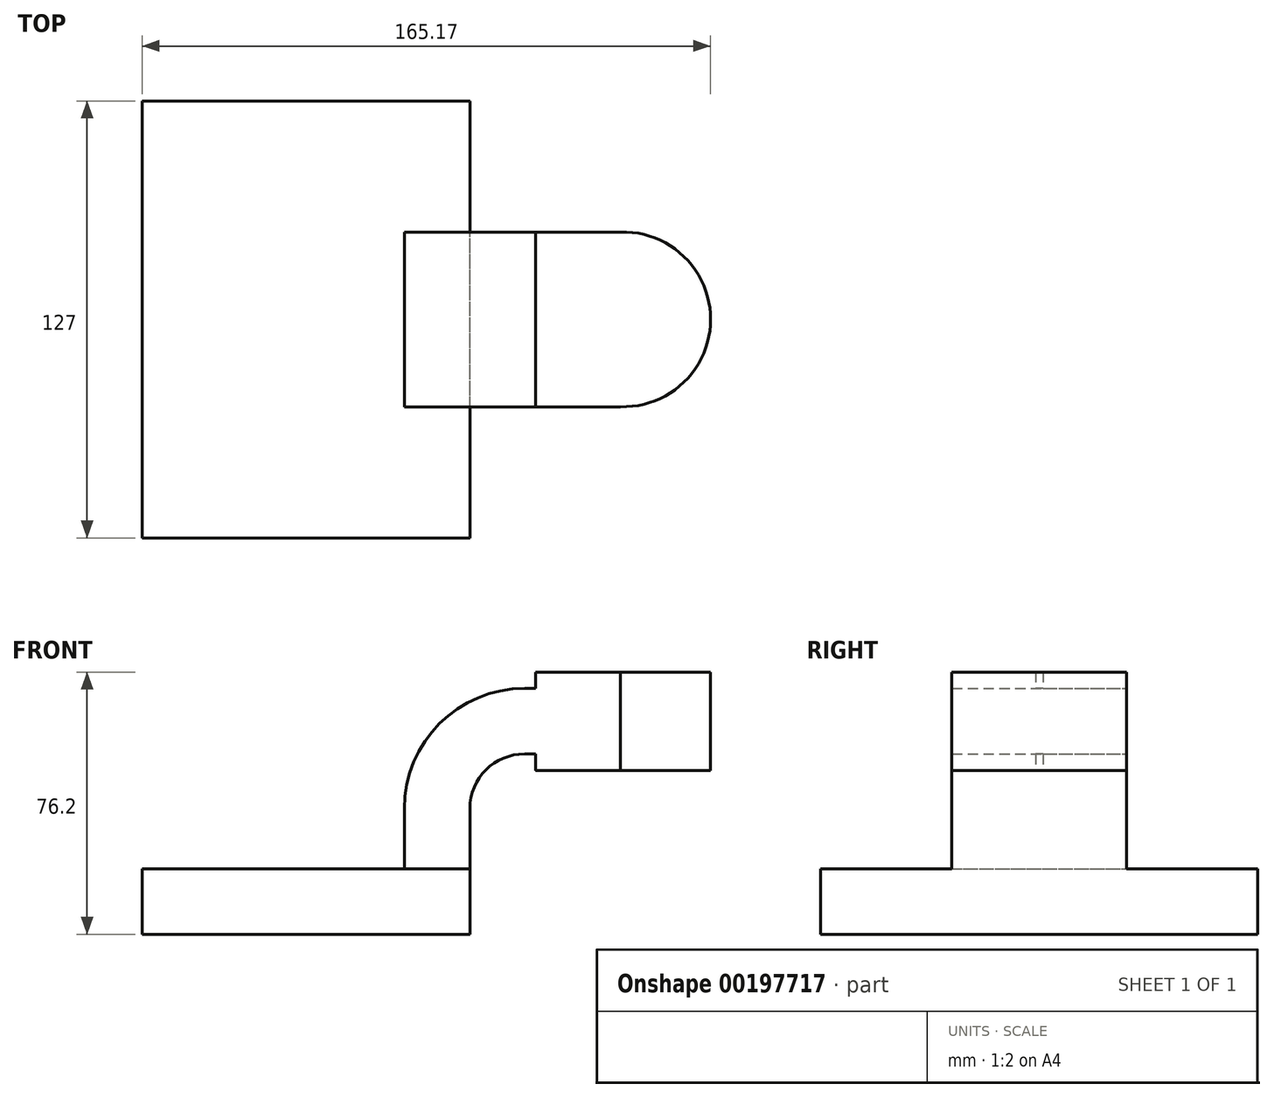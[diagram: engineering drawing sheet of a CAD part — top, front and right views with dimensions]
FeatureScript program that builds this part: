
annotation { "Feature Type Name" : "Feature", "Feature Type Description" : "" }
export const myFeature = defineFeature(function(context is Context, id is Id, definition is map)
    precondition{}
    {
        {
            var Q0;
            Q0=qCreatedBy(makeId("Front.planeOp"),FACE);
            var sketch = newSketch(context, id + "F0", { "sketchPlane" : qUnion([Q0])});
            skLineSegment(sketch, "E0.bottom", {"start": v(-47.62, 9.52) * mm, "end": v(47.62, 9.52) * mm});
            skLineSegment(sketch, "E0.top", {"start": v(-47.62, -9.53) * mm, "end": v(47.62, -9.53) * mm});
            skLineSegment(sketch, "E0.left", {"start": v(-47.62, 9.52) * mm, "end": v(-47.62, -9.53) * mm});
            skLineSegment(sketch, "E0.right", {"start": v(47.62, 9.52) * mm, "end": v(47.63, -9.52) * mm});
            skPoint(sketch, "E0.middle", {"position": v(0, 0) * mm});
            skLineSegment(sketch, "E1", {"start": v(47.62, 9.52) * mm, "end": v(47.62, 27) * mm});
            skArc(sketch, "E2", {"start": v(47.62, 27) * mm, "mid": v(52.27, 38.23) * mm, "end": v(63.5, 42.88) * mm});
            skLineSegment(sketch, "E3", {"start": v(63.5, 42.88) * mm, "end": v(92.08, 42.88) * mm});
            skLineSegment(sketch, "E4.bottom", {"start": v(117.55, 38.1) * mm, "end": v(66.75, 38.1) * mm});
            skLineSegment(sketch, "E4.top", {"start": v(117.55, 66.68) * mm, "end": v(66.75, 66.68) * mm});
            skLineSegment(sketch, "E4.left", {"start": v(117.55, 38.1) * mm, "end": v(117.55, 66.67) * mm});
            skLineSegment(sketch, "E4.right", {"start": v(66.75, 38.1) * mm, "end": v(66.75, 66.67) * mm});
            skPoint(sketch, "E4.middle", {"position": v(92.15, 52.39) * mm});
            skLineSegment(sketch, "E5.0", {"start": v(63.5, 61.93) * mm, "end": v(92.08, 61.93) * mm});
            skArc(sketch, "E5.1", {"start": v(28.58, 27) * mm, "mid": v(38.8, 51.7) * mm, "end": v(63.5, 61.93) * mm});
            skLineSegment(sketch, "E5.2", {"start": v(28.58, 9.52) * mm, "end": v(28.58, 27) * mm});
            skLineSegment(sketch, "E6", {"start": v(92.14, 38.1) * mm, "end": v(92.14, 66.68) * mm});
            skFitSpline(sketch, "E7", {"points": [v(-47.62, 9.52) * mm, v(63.5, 61.93) * mm], "startDerivative": vector(51.78, 123.38) * mm, "endDerivative": vector(113.37, -4.4) * mm});
            skSolve(sketch);
        }
        {
            var Q0;
            Q0=makeQuery(id+"F0.imprint","IMPRINT",FACE,{"disambiguationData":[TD([[makeQuery(id+"F0.imprint","IMPRINT",EDGE,{"derivedFrom":sQuery(id+"F0.wireOp",EDGE,"E0.top")}),1.0]])]});
            extrude(context, id + "F1", {"entities" : qUnion([Q0]), "endBound" : BoundingType.SYMMETRIC, "depth" : 127 * mm});
        }
        {
            var Q0;
            {var subQ8=sQuery(id+"F0.wireOp",EDGE,"E1");Q0=makeQuery(id+"F0.imprint","IMPRINT",FACE,{"disambiguationData":[TD([[makeQuery(id+"F0.imprint","IMPRINT",EDGE,{"derivedFrom":subQ8}),1.0]])]});}
            extrude(context, id + "F2", {"entities" : qUnion([Q0]), "operationType" : NewBodyOperationType.ADD, "endBound" : BoundingType.SYMMETRIC, "depth" : 50.8 * mm});
        }
        {
            var Q0;
            {var subQ7=sQuery(id+"F0.wireOp",EDGE,"E6");Q0=makeQuery(id+"F0.imprint","IMPRINT",FACE,{"disambiguationData":[TD([[makeQuery(id+"F0.imprint","IMPRINT",EDGE,{"derivedFrom":subQ7}),1.0]])]});}
            extrude(context, id + "F3", {"entities" : qUnion([Q0]), "operationType" : NewBodyOperationType.ADD, "endBound" : BoundingType.SYMMETRIC, "depth" : 50.8 * mm});
        }
        {
            var Q0;
            Q0=makeQuery(id+"F0.imprint","IMPRINT",FACE,{"disambiguationData":[TD([[makeQuery(id+"F0.imprint","IMPRINT",EDGE,{"derivedFrom":sQuery(id+"F0.wireOp",EDGE,"E5.1")}),1.0]])]});
            extrude(context, id + "F4", {"entities" : qUnion([Q0]), "operationType" : NewBodyOperationType.ADD, "endBound" : BoundingType.SYMMETRIC, "depth" : 15.88 * mm});
        }
        {
            var Q0;
            {var subQ0=sQuery(id+"F0.wireOp",EDGE,"E4.left");Q0=makeQuery(id+"F0.imprint","IMPRINT",FACE,{"disambiguationData":[TD([[makeQuery(id+"F0.imprint","IMPRINT",EDGE,{"derivedFrom":subQ0}),1.0]])]});}
            var Q1;
            Q1=sQuery(id+"F0.wireOp",EDGE,"E6");
            revolve(context, id + "F5", {"operationType" : NewBodyOperationType.ADD, "entities" : qUnion([Q0]), "axis" : qUnion([Q1]), "revolveType" : RevolveType.SYMMETRIC, "angle" : 360 * degree});
        }
    });
